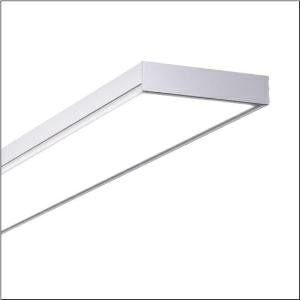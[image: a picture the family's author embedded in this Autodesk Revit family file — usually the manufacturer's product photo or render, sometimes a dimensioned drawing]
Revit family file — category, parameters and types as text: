
# Revit family: apollon_31_surface_51mp26wd2341e
name_source: partatom
category: Lighting Fixtures
units: mm (PartAtom-declared; Revit-internal decimal feet)

## family parameters
Cut with Voids When Loaded = No
Host = Face
Light Source = No
Part Type = Normal
Room Calculation Point = No
Round Connector Dimension = Use Diameter
Shared = No

## types (1)
- Apollon 31 Surface (1 x LED, 4400 lm, 33 W, 3000K)
    Apparent Load = 33 VA
    CIE Flux Codes = 61 87 97 97 100
    Color Rendering = 80
    Color Temperature = 3000K
    Default Elevation = 1800 mm
    Description = Apollon 31 Surface, office luminaire, primary optical cover: micro prismatic cover, of PMMA, light emission: direct distribution, primary light characteristic: symmetric, installation type: surface-mounted, LED, rated luminous flux: 4.400lm, luminous efficacy: 133lm/W, light colour: 830, colour temperature: 3000K, control gear: DALI 2, with terminal, 5-pole, mains connection: 220..240V, AC, 50/60Hz, rated input power: 33W, housing, of sheet steel, coated, metallic grey (RAL 9006), length: 1.545mm, width: 200mm, height: 44mm, protection rating (complete): IP20, protection rating (on room side): IP40, protection rating (lamp compartment, on room side): IP40, insulation class (complete): insulation class I (protective earthing), certification: CE, ENEC, UKCA, impact resistance: IK02, permissible operating ambient temperature: -20..+40°C, standard: EN 60598-2-22, packaging unit: 1 piece
    Height = 44 mm
    Lamp = 1 x LED
    Lamp Light Flux = 4400 lm
    Lamp Power = 33 W
    Lamp count = 1
    Length = 1545 mm
    Luminous efficacy = 133 lm/W
    Manufacturer = Siteco
    ModVariant = No
    Model = 51MP26WD2341E
    Mounting Place = Ceiling
    Mounting Type = Surface mounted
    Number of Poles = 1
    OnlyDefault = Yes
    Power Factor = 1
    Product Name = Apollon 31 Surface
    Product group = office luminaire | ceiling mounted
    ProductGroupID = 301
    Protection Class = Protection class I
    Protection Degree = IP 20
    RLX_Detail_Level = 1
    RLX_Emergency_Light_Flux = 0 lm
    RLX_Emergency_Type = 0
    RLX_Emergency_Type_DB = No
    RlxData = <blob elided: 24149 chars, md5=c27426b9>
    Socket = socket
    Standby Power = 0 W
    System Light Flux = 4400 lm
    System Power = 33 W
    Type Comments = Product without accessories
    Type Image = l_1313654.jpg
    URL = http://relux.com
    VarID = ---
    Voltage = 0 V
    Weight = 0.00 kg
    Width = 200 mm  [stored 0.656168 ft]

note: [stored X ft] marks values corroborated as IEEE doubles in the binary element streams (Revit-internal decimal feet)

## geometry (parser evidence)
native form markers: Blend x4, Sweep x10
no freeform markers — native parametric forms only
